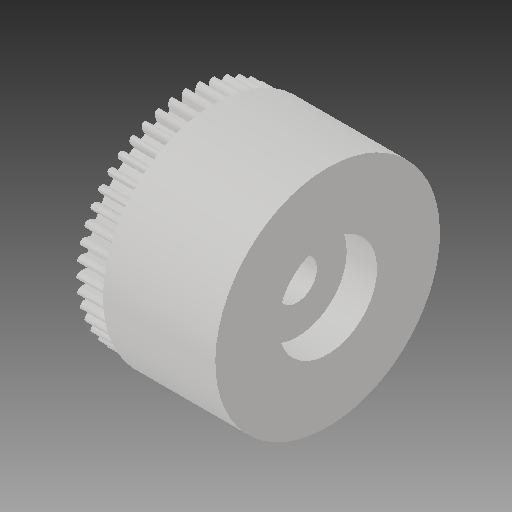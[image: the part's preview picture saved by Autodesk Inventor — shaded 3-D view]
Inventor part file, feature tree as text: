
AUTODESK INVENTOR PART (.ipt)
format: ipt  version: 2018 (Build 220112000, 112)  size: 649,216 bytes
history: native  units: in
note: dims shown in document units (in); Inventor stores cm internally (conversion verified against a paired STEP export)
features: sketch x7, extrude x6
ambient origin geometry x8: Origin, YZ Plane, XZ Plane, XY Plane, X Axis, Y Axis, Z Axis, Center Point
bodies: Solid1 (feature_tree)
feature tree (13):
  extrude  "Extrusion1"  Depth=1.0in TaperAngle=0.0deg
  extrude  "Extrusion2"  Depth=0.27in TaperAngle=0.0deg
  extrude  "Extrusion3"  Depth=0.27in TaperAngle=0.0deg
  extrude  "Extrusion7"  Depth=0.2756in TaperAngle=0.0deg
  extrude  "Extrusion8"  Depth=0.3937in TaperAngle=0.0deg
  sketch  "Sketch6"  dims[d51=0.88in d52=0.3937in d53=0.0in]
  extrude  "Extrusion9"  Depth=0.3937in TaperAngle=0.0deg
  sketch  "Sketch1"  dims[d3=0.35in d4=1.0in d5=0.0in]
  sketch  "Sketch2"  dims[d6=0.865in d7=0.27in d8=0.0in]
  sketch  "Sketch3"  dims[d9=0.865in d10=0.27in d11=0.0in]
  sketch  "Sketch4"  dims[d40=18.8976in d42=360.0deg d46=0.2756in d47=0.0in]
  sketch  "Sketch5"  dims[d48=0.88in d49=0.3937in d50=0.0in]
  sketch  "Sketch7"
